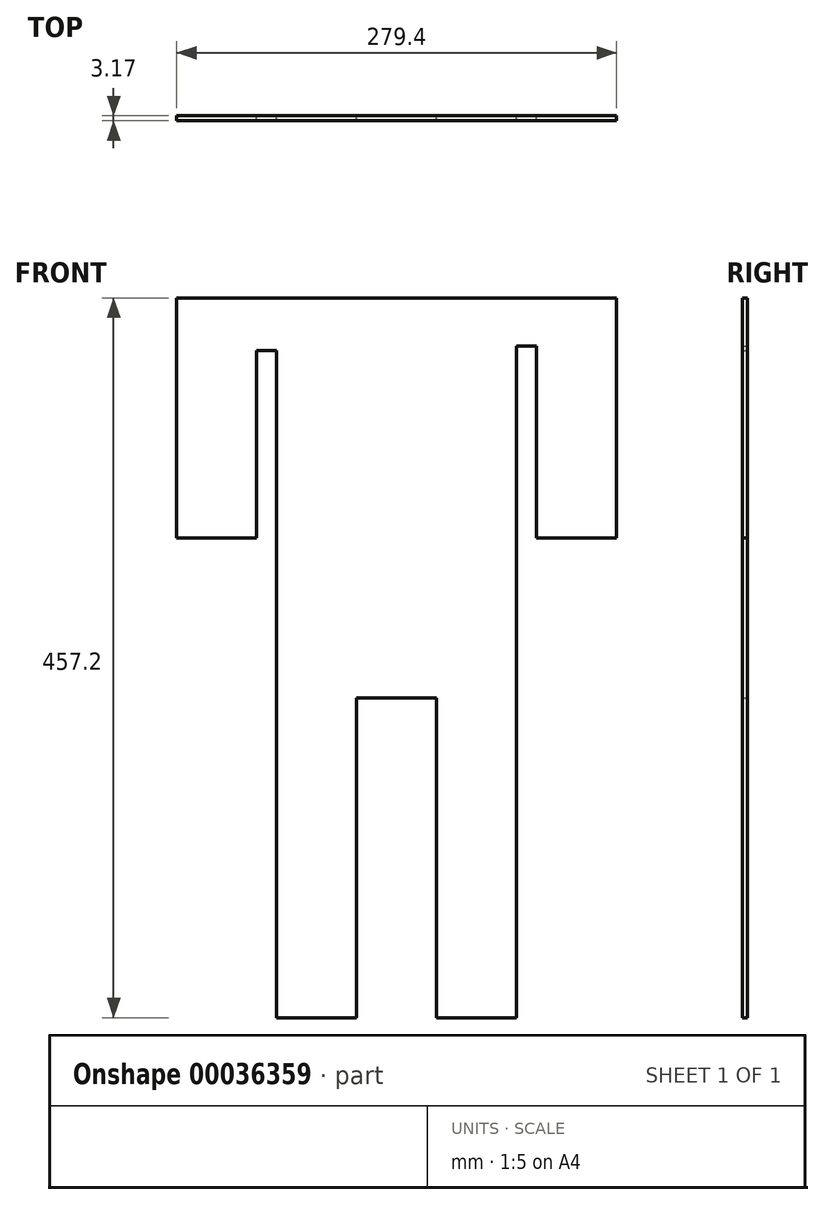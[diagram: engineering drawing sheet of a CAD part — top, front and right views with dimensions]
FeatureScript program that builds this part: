
annotation { "Feature Type Name" : "Feature", "Feature Type Description" : "" }
export const myFeature = defineFeature(function(context is Context, id is Id, definition is map)
    precondition{}
    {
        {
            var Q0;
            Q0=qCreatedBy(makeId("Front.planeOp"),FACE);
            var sketch = newSketch(context, id + "F0", { "sketchPlane" : qUnion([Q0])});
            skLineSegment(sketch, "E0.bottom", {"start": v(-300.05, 66.9) * mm, "end": v(-249.25, 66.9) * mm});
            skLineSegment(sketch, "E0.top", {"start": v(-300.05, -136.3) * mm, "end": v(-249.25, -136.3) * mm});
            skLineSegment(sketch, "E0.left", {"start": v(-300.05, 66.9) * mm, "end": v(-300.05, -136.3) * mm});
            skLineSegment(sketch, "E0.right", {"start": v(-249.25, 66.9) * mm, "end": v(-249.25, -136.3) * mm});
            skLineSegment(sketch, "E1.bottom", {"start": v(-300.05, 66.9) * mm, "end": v(-147.65, 66.9) * mm});
            skLineSegment(sketch, "E1.top", {"start": v(-300.05, 117.7) * mm, "end": v(-147.65, 117.7) * mm});
            skLineSegment(sketch, "E1.left", {"start": v(-300.05, 66.9) * mm, "end": v(-300.05, 117.7) * mm});
            skLineSegment(sketch, "E1.right", {"start": v(-147.65, 66.9) * mm, "end": v(-147.65, 117.7) * mm});
            skLineSegment(sketch, "E2.bottom", {"start": v(-147.65, 66.9) * mm, "end": v(-198.45, 66.9) * mm});
            skLineSegment(sketch, "E2.top", {"start": v(-147.65, -136.3) * mm, "end": v(-198.45, -136.3) * mm});
            skLineSegment(sketch, "E2.left", {"start": v(-147.65, 66.9) * mm, "end": v(-147.65, -136.3) * mm});
            skLineSegment(sketch, "E2.right", {"start": v(-198.45, 66.9) * mm, "end": v(-198.45, -136.3) * mm});
            skLineSegment(sketch, "E3.top", {"start": v(-300.05, 320.9) * mm, "end": v(-147.65, 320.9) * mm});
            skLineSegment(sketch, "E3.left", {"start": v(-300.05, 117.7) * mm, "end": v(-300.05, 320.9) * mm});
            skLineSegment(sketch, "E3.right", {"start": v(-147.65, 117.7) * mm, "end": v(-147.65, 320.9) * mm});
            skLineSegment(sketch, "E4.bottom", {"start": v(-300.05, 320.9) * mm, "end": v(-312.75, 320.9) * mm});
            skLineSegment(sketch, "E4.top", {"start": v(-300.05, 287.34) * mm, "end": v(-312.75, 287.34) * mm});
            skLineSegment(sketch, "E4.left", {"start": v(-300.05, 320.9) * mm, "end": v(-300.05, 287.34) * mm});
            skLineSegment(sketch, "E4.right", {"start": v(-312.75, 320.9) * mm, "end": v(-312.75, 287.34) * mm});
            skLineSegment(sketch, "E5.bottom", {"start": v(-147.65, 320.9) * mm, "end": v(-134.95, 320.9) * mm});
            skLineSegment(sketch, "E5.top", {"start": v(-147.65, 290.3) * mm, "end": v(-134.95, 290.3) * mm});
            skLineSegment(sketch, "E5.left", {"start": v(-147.65, 320.9) * mm, "end": v(-147.65, 290.3) * mm});
            skLineSegment(sketch, "E5.right", {"start": v(-134.95, 320.9) * mm, "end": v(-134.95, 290.3) * mm});
            skLineSegment(sketch, "E6.bottom", {"start": v(-312.75, 320.9) * mm, "end": v(-363.55, 320.9) * mm});
            skLineSegment(sketch, "E6.top", {"start": v(-312.75, 168.5) * mm, "end": v(-363.55, 168.5) * mm});
            skLineSegment(sketch, "E6.left", {"start": v(-312.75, 320.9) * mm, "end": v(-312.75, 168.5) * mm});
            skLineSegment(sketch, "E6.right", {"start": v(-363.55, 320.9) * mm, "end": v(-363.55, 168.5) * mm});
            skLineSegment(sketch, "E7.bottom", {"start": v(-134.95, 320.9) * mm, "end": v(-84.15, 320.9) * mm});
            skLineSegment(sketch, "E7.top", {"start": v(-134.95, 168.5) * mm, "end": v(-84.15, 168.5) * mm});
            skLineSegment(sketch, "E7.left", {"start": v(-134.95, 320.9) * mm, "end": v(-134.95, 168.5) * mm});
            skLineSegment(sketch, "E7.right", {"start": v(-84.15, 320.9) * mm, "end": v(-84.15, 168.5) * mm});
            skSolve(sketch);
        }
        {
            var Q0;
            Q0 = qSketchRegion(id + "F0", true);
            extrude(context, id + "F1", {"entities" : qUnion([Q0]), "depth" : 3.17 * mm});
        }
        {
            var Q0;
            Q0=qCreatedBy(makeId("Front.planeOp"),FACE);
            cPlane(context, id + "F2", {"entities" : qUnion([Q0]), "cplaneType" : CPlaneType.OFFSET, "offset" : 152.4 * mm, "width" : 152.4 * mm, "height" : 152.4 * mm});
        }
    });
